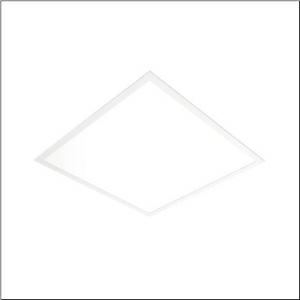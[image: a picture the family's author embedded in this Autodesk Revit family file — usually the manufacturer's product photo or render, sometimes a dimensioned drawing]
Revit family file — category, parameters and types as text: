
# Revit family: apollon_r__41_51mh11wd2443_7c66
name_source: partatom
category: Lighting Fixtures
units: mm (PartAtom-declared; Revit-internal decimal feet)

## family parameters
Cut with Voids When Loaded = No
Host = Face
Light Source = No
Part Type = Normal
Room Calculation Point = No
Round Connector Dimension = Use Diameter
Shared = No

## types (1)
- Apollon® 41 (1 x LED, 3500 lm, 28.5 W, 4000K)
    Apparent Load = 29 VA
    CIE Flux Codes = 61 87 97 100 100
    Color Rendering = 80
    Color Temperature = 4000K
    Default Elevation = 1800 mm
    Description = Apollon® 41, office luminaire, primary optical cover: prismatic diffuser, of PS, light emission: direct distribution, primary light characteristic: symmetric, installation type: lay-in mounting, LED, rated luminous flux: 3.500lm, luminous efficacy: 123lm/W, light colour: 840, colour temperature: 4000K, control gear: DALI 2, with terminal, 5-pole, mains connection: 220..240V, AC, 50/60Hz, suitable for self-contained emergency lighting element 58DB00B013A with integrated self-test function according to EN 60598-2-22, housing, of aluminium section, traffic white (RAL 9016), module: M625, length: 620mm, width: 620mm, height: 60mm, recess depth: 180mm, housing upper side, of sheet steel, protection rating (complete): IP20, protection rating (lamp compartment, on room side): IP40, insulation class (complete): insulation class II (safety insulation), certification: CE, ENEC, impact resistance: IK03, permissible operating ambient temperature: -25..+40°C, packaging unit: 1 piece
    Height = 0 mm  [stored 0 ft]
    Lamp = 1 x LED
    Lamp Light Flux = 3500 lm
    Lamp Power = 28.5 W
    Lamp count = 1
    Length = 620 mm
    Luminous efficacy = 123 lm/W
    Manufacturer = Siteco
    ModVariant = No
    Model = 51MH11WD2443
    Mounting Place = Ceiling
    Mounting Type = Recessed
    Number of Poles = 1
    OnlyDefault = Yes
    Power Factor = 1
    Product Name = Apollon® 41
    Product group = office luminaire | ceiling recessed
    ProductGroupID = 400
    Protection Class = Protection class II
    Protection Degree = IP 20
    RLX_Detail_Level = 1
    RLX_Emergency_Light_Flux = 0 lm
    RLX_Emergency_Type = 0
    RLX_Emergency_Type_DB = No
    RlxData = <blob elided: 12425 chars, md5=f2f60a51>
    Socket = socket
    Standby Power = 0 W
    System Light Flux = 3500 lm
    System Power = 29 W
    Type Comments = Product without accessories
    Type Image = l_1291024.jpg
    URL = http://relux.com
    VarID = ---
    Voltage = 0 V
    Weight = 0.00 kg
    Width = 620 mm

note: [stored X ft] marks values corroborated as IEEE doubles in the binary element streams (Revit-internal decimal feet)

## geometry (parser evidence)
native form markers: Sweep x11
no freeform markers — native parametric forms only
